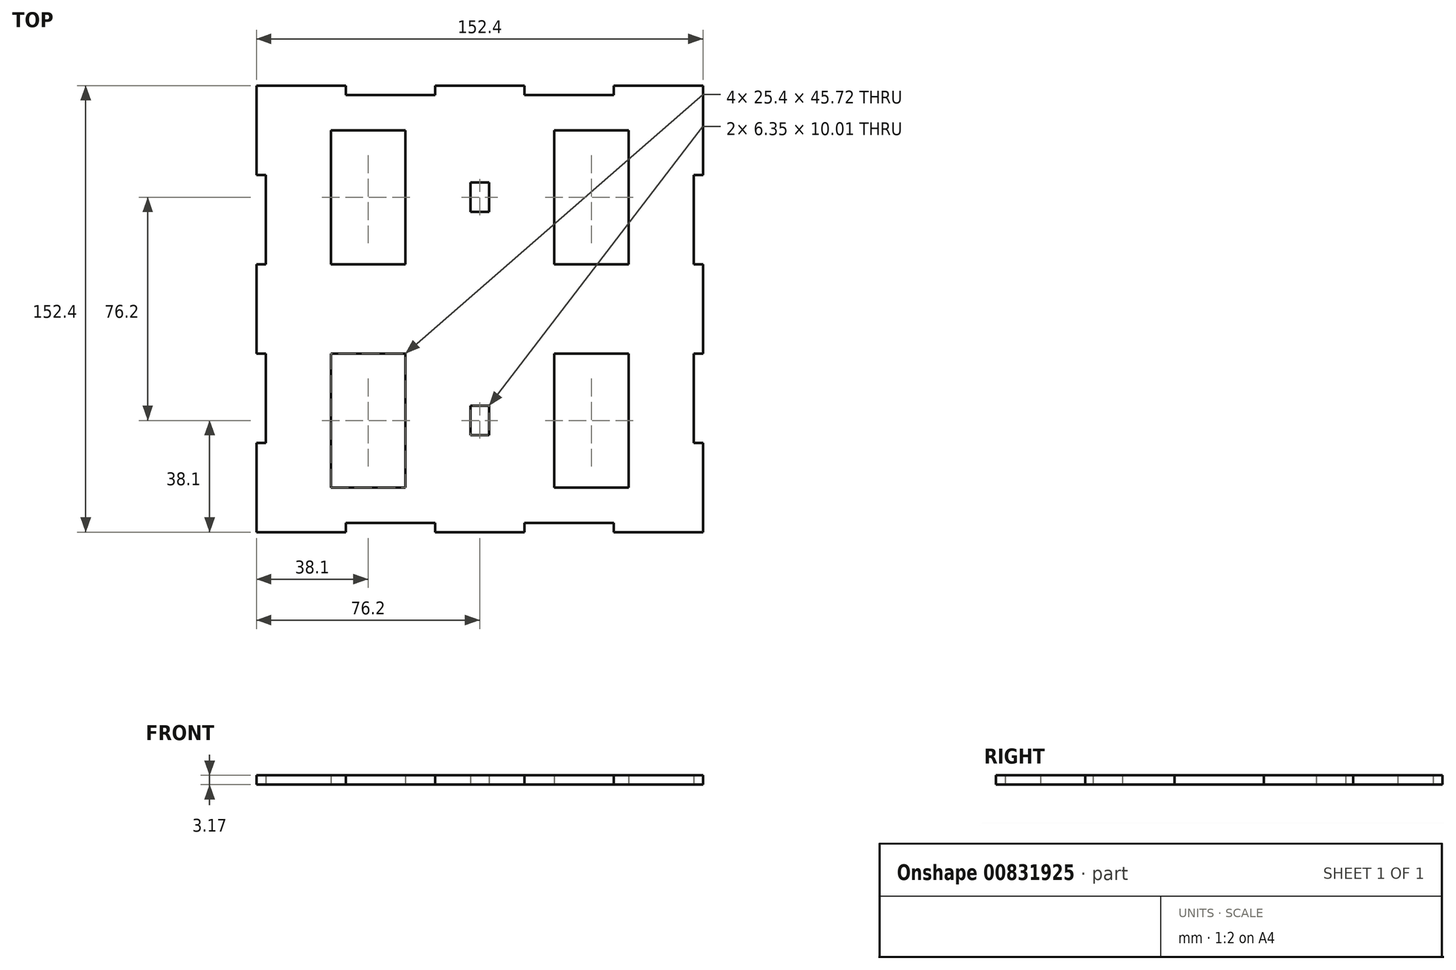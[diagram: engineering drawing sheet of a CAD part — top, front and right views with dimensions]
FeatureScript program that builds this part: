
annotation { "Feature Type Name" : "Feature", "Feature Type Description" : "" }
export const myFeature = defineFeature(function(context is Context, id is Id, definition is map)
    precondition{}
    {
        {
            var Q0;
            Q0=qCreatedBy(makeId("Top.planeOp"),FACE);
            var sketch = newSketch(context, id + "F0", { "sketchPlane" : qUnion([Q0])});
            skLineSegment(sketch, "E0.bottom", {"start": v(-76.2, 76.2) * mm, "end": v(-45.72, 76.2) * mm});
            skLineSegment(sketch, "E0.top", {"start": v(-76.2, -76.2) * mm, "end": v(-45.72, -76.2) * mm});
            skLineSegment(sketch, "E0.left", {"start": v(-76.2, 76.2) * mm, "end": v(-76.2, 45.72) * mm});
            skLineSegment(sketch, "E0.right", {"start": v(76.2, 76.2) * mm, "end": v(76.2, 45.72) * mm});
            skPoint(sketch, "E1", {"position": v(0, 0) * mm});
            skPoint(sketch, "E1.positionSnap0", {"position": v(0, 76.2) * mm});
            skPoint(sketch, "E1.positionSnap1", {"position": v(-76.2, 0) * mm});
            skLineSegment(sketch, "E2", {"start": v(-45.72, 76.2) * mm, "end": v(-45.72, 73.03) * mm});
            skLineSegment(sketch, "E3", {"start": v(-45.72, 73.03) * mm, "end": v(-15.24, 73.03) * mm});
            skLineSegment(sketch, "E4", {"start": v(-15.24, 73.03) * mm, "end": v(-15.24, 76.2) * mm});
            skLineSegment(sketch, "E5", {"start": v(15.24, 76.2) * mm, "end": v(15.24, 73.03) * mm});
            skLineSegment(sketch, "E6", {"start": v(15.24, 73.03) * mm, "end": v(45.72, 73.03) * mm});
            skLineSegment(sketch, "E7", {"start": v(45.72, 73.03) * mm, "end": v(45.72, 76.2) * mm});
            skLineSegment(sketch, "E8", {"start": v(45.72, 76.2) * mm, "end": v(76.2, 76.2) * mm});
            skLineSegment(sketch, "E9", {"start": v(-76.2, 45.72) * mm, "end": v(-73.03, 45.72) * mm});
            skLineSegment(sketch, "E10", {"start": v(-73.03, 45.72) * mm, "end": v(-73.03, 15.24) * mm});
            skLineSegment(sketch, "E11", {"start": v(-73.03, 15.24) * mm, "end": v(-76.2, 15.24) * mm});
            skLineSegment(sketch, "E12", {"start": v(-76.2, 15.24) * mm, "end": v(-76.2, -15.24) * mm});
            skLineSegment(sketch, "E13", {"start": v(-76.2, -15.24) * mm, "end": v(-73.02, -15.24) * mm});
            skLineSegment(sketch, "E14", {"start": v(-73.02, -15.24) * mm, "end": v(-73.02, -45.72) * mm});
            skLineSegment(sketch, "E15", {"start": v(-73.02, -45.72) * mm, "end": v(-76.2, -45.72) * mm});
            skLineSegment(sketch, "E16", {"start": v(-76.2, -45.72) * mm, "end": v(-76.2, -76.2) * mm});
            skLineSegment(sketch, "E17", {"start": v(-45.72, -76.2) * mm, "end": v(-45.72, -73.03) * mm});
            skLineSegment(sketch, "E18", {"start": v(-45.72, -73.02) * mm, "end": v(-15.24, -73.02) * mm});
            skLineSegment(sketch, "E19", {"start": v(-15.24, -73.03) * mm, "end": v(-15.24, -76.2) * mm});
            skLineSegment(sketch, "E20", {"start": v(-15.24, -76.2) * mm, "end": v(15.24, -76.2) * mm});
            skLineSegment(sketch, "E21", {"start": v(15.24, -76.2) * mm, "end": v(15.24, -73.02) * mm});
            skLineSegment(sketch, "E22", {"start": v(15.24, -73.02) * mm, "end": v(45.72, -73.02) * mm});
            skLineSegment(sketch, "E23", {"start": v(45.72, -73.02) * mm, "end": v(45.72, -76.2) * mm});
            skLineSegment(sketch, "E24", {"start": v(45.72, -76.2) * mm, "end": v(76.2, -76.2) * mm});
            skLineSegment(sketch, "E25", {"start": v(76.2, -76.2) * mm, "end": v(76.2, -45.72) * mm});
            skLineSegment(sketch, "E26", {"start": v(76.2, -45.72) * mm, "end": v(73.03, -45.72) * mm});
            skLineSegment(sketch, "E27", {"start": v(73.03, -45.72) * mm, "end": v(73.03, -15.24) * mm});
            skLineSegment(sketch, "E28", {"start": v(73.03, -15.24) * mm, "end": v(76.2, -15.24) * mm});
            skLineSegment(sketch, "E29", {"start": v(76.2, -15.24) * mm, "end": v(76.2, 15.24) * mm});
            skLineSegment(sketch, "E30", {"start": v(76.2, 15.24) * mm, "end": v(73.02, 15.24) * mm});
            skLineSegment(sketch, "E31", {"start": v(73.02, 15.24) * mm, "end": v(73.02, 45.72) * mm});
            skLineSegment(sketch, "E32", {"start": v(73.02, 45.72) * mm, "end": v(76.2, 45.72) * mm});
            skLineSegment(sketch, "E33", {"start": v(76.2, 45.72) * mm, "end": v(76.2, 76.2) * mm});
            skLineSegment(sketch, "E34.trimOffspring", {"start": v(-15.24, 76.2) * mm, "end": v(15.24, 76.2) * mm});
            skLineSegment(sketch, "E35.trimOffspring", {"start": v(76.2, 15.24) * mm, "end": v(76.2, -76.2) * mm});
            skLineSegment(sketch, "E36.bottom", {"start": v(-50.8, 60.96) * mm, "end": v(-25.4, 60.96) * mm});
            skLineSegment(sketch, "E36.top", {"start": v(-50.8, 15.24) * mm, "end": v(-25.4, 15.24) * mm});
            skLineSegment(sketch, "E36.left", {"start": v(-50.8, 60.96) * mm, "end": v(-50.8, 15.24) * mm});
            skLineSegment(sketch, "E36.right", {"start": v(-25.4, 60.96) * mm, "end": v(-25.4, 15.24) * mm});
            skLineSegment(sketch, "E37.bottom", {"start": v(-50.8, -15.24) * mm, "end": v(-25.4, -15.24) * mm});
            skLineSegment(sketch, "E37.top", {"start": v(-50.8, -60.96) * mm, "end": v(-25.4, -60.96) * mm});
            skLineSegment(sketch, "E37.left", {"start": v(-50.8, -15.24) * mm, "end": v(-50.8, -60.96) * mm});
            skLineSegment(sketch, "E37.right", {"start": v(-25.4, -15.24) * mm, "end": v(-25.4, -60.96) * mm});
            skLineSegment(sketch, "E38.bottom", {"start": v(25.4, 60.96) * mm, "end": v(50.8, 60.96) * mm});
            skLineSegment(sketch, "E38.top", {"start": v(25.4, 15.24) * mm, "end": v(50.8, 15.24) * mm});
            skLineSegment(sketch, "E38.left", {"start": v(25.4, 60.96) * mm, "end": v(25.4, 15.24) * mm});
            skLineSegment(sketch, "E38.right", {"start": v(50.8, 60.96) * mm, "end": v(50.8, 15.24) * mm});
            skLineSegment(sketch, "E39.bottom", {"start": v(25.4, -15.24) * mm, "end": v(50.8, -15.24) * mm});
            skLineSegment(sketch, "E39.top", {"start": v(25.4, -60.96) * mm, "end": v(50.8, -60.96) * mm});
            skLineSegment(sketch, "E39.left", {"start": v(25.4, -15.24) * mm, "end": v(25.4, -60.96) * mm});
            skLineSegment(sketch, "E39.right", {"start": v(50.8, -15.24) * mm, "end": v(50.8, -60.96) * mm});
            skLineSegment(sketch, "E40.bottom", {"start": v(-3.18, 43.1) * mm, "end": v(3.17, 43.1) * mm});
            skLineSegment(sketch, "E40.top", {"start": v(-3.18, 33.1) * mm, "end": v(3.17, 33.1) * mm});
            skLineSegment(sketch, "E40.left", {"start": v(-3.18, 43.1) * mm, "end": v(-3.18, 33.1) * mm});
            skLineSegment(sketch, "E40.right", {"start": v(3.17, 43.1) * mm, "end": v(3.17, 33.1) * mm});
            skLineSegment(sketch, "E41.bottom", {"start": v(-3.18, -33.1) * mm, "end": v(3.17, -33.1) * mm});
            skLineSegment(sketch, "E41.top", {"start": v(-3.18, -43.1) * mm, "end": v(3.17, -43.1) * mm});
            skLineSegment(sketch, "E41.left", {"start": v(-3.18, -33.1) * mm, "end": v(-3.18, -43.1) * mm});
            skLineSegment(sketch, "E41.right", {"start": v(3.17, -33.1) * mm, "end": v(3.17, -43.1) * mm});
            skSolve(sketch);
        }
        {
            var Q0;
            Q0=makeQuery(id+"F0.imprint","IMPRINT",FACE,{"disambiguationData":[TD([[makeQuery(id+"F0.imprint","IMPRINT",EDGE,{"derivedFrom":sQuery(id+"F0.wireOp",EDGE,"E0.bottom")}),-1.0]])]});
            extrude(context, id + "F1", {"entities" : qUnion([Q0]), "depth" : 3.17 * mm, "offsetDistance" : 25.4 * mm});
        }
    });
